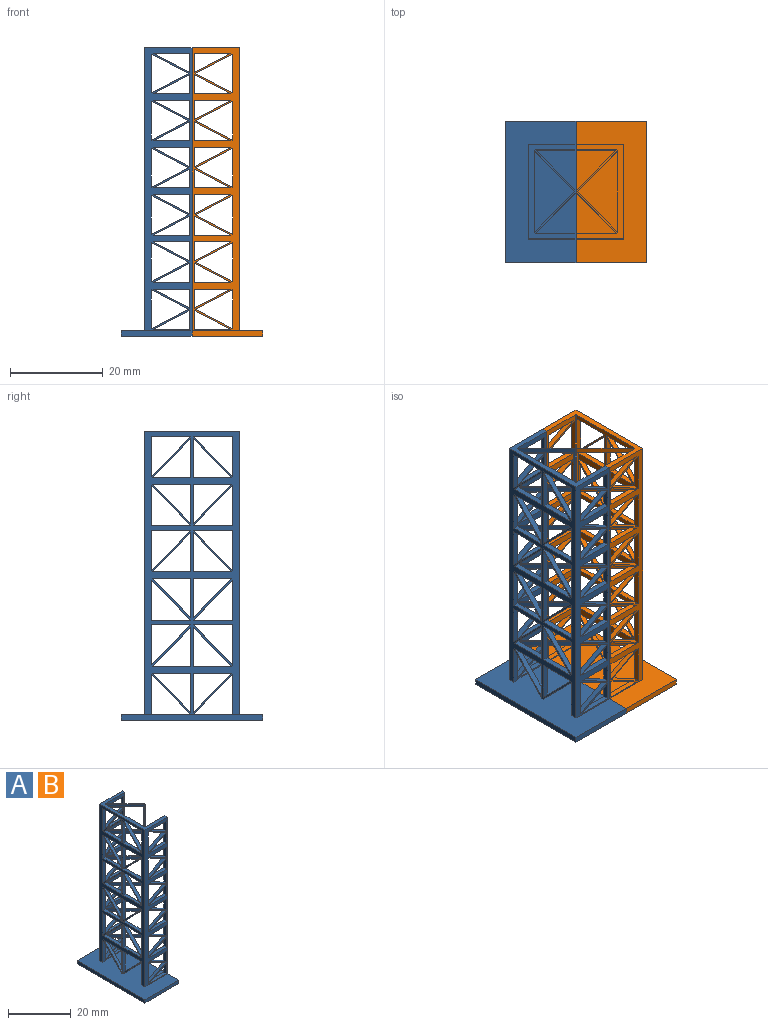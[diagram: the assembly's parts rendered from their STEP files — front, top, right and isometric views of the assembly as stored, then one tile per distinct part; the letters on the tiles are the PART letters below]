
ASSEMBLY  parts=2 mates=1
PART A: 257 faces, bbox 20000000000000000038313501714693374724319102545303840223056070291987586484079775119224722902163606470656x20000000000000000038313501714693374724319102545303840223056070291987586484079775119224722902163606470656x62.2 mm
  f0: plane 7.77x1.16mm, normal (0,0,-1), area 9mm2, adj f1,f253,f254,f255
  f1: plane 60.96x10.16mm, normal (0,1,0), area 227.5mm2, adj f0,f2,f3,f4,f5,f6,f7,f8
  f2: plane 8.02x4.2mm, normal (-0.46,0,0.89), area 10.5mm2, adj f1,f3,f4,f254
  f3: plane 8.4x1.16mm, normal (1,0,0), area 9.7mm2, adj f1,f2,f4,f254
  f4: plane 8.02x4.2mm, normal (-0.46,0,-0.89), area 10.5mm2, adj f1,f2,f3,f254
  f5: plane 8.4x1.16mm, normal (1,0,0), area 9.7mm2, adj f1,f6,f7,f254
  f6: plane 8.02x4.2mm, normal (-0.46,0,-0.89), area 10.5mm2, adj f1,f5,f7,f254
  f7: plane 8.02x4.2mm, normal (-0.46,0,0.89), area 10.5mm2, adj f1,f5,f6,f254
  f8: plane 8.4x1.16mm, normal (1,0,0), area 9.7mm2, adj f1,f9,f10,f254
  f9: plane 8.02x4.2mm, normal (-0.46,0,-0.89), area 10.5mm2, adj f1,f8,f10,f254
  f10: plane 8.02x4.2mm, normal (-0.46,0,0.89), area 10.5mm2, adj f1,f8,f9,f254
  f11: plane 8.4x1.16mm, normal (1,0,0), area 9.7mm2, adj f1,f12,f13,f254
  f12: plane 8.02x4.2mm, normal (-0.46,0,-0.89), area 10.5mm2, adj f1,f11,f13,f254
  f13: plane 8.02x4.2mm, normal (-0.46,0,0.89), area 10.5mm2, adj f1,f11,f12,f254
  f14: plane 8.02x4.2mm, normal (-0.46,0,-0.89), area 10.5mm2, adj f1,f15,f16,f254
  f15: plane 8.02x4.2mm, normal (-0.46,0,0.89), area 10.5mm2, adj f1,f14,f16,f254
  f16: plane 8.4x1.16mm, normal (1,0,0), area 9.7mm2, adj f1,f14,f15,f254
  f17: plane 8.02x4.2mm, normal (-0.46,0,-0.89), area 10.5mm2, adj f1,f18,f19,f254
  f18: plane 8.02x4.2mm, normal (-0.46,0,0.89), area 10.5mm2, adj f1,f17,f19,f254
  f19: plane 8.4x1.16mm, normal (1,0,0), area 9.7mm2, adj f1,f17,f18,f254
  f20: plane 7.77x1.16mm, normal (0,0,1), area 9mm2, adj f1,f21,f22,f254
  f21: plane 7.77x4.07mm, normal (0.46,0,-0.89), area 10.2mm2, adj f1,f20,f22,f254
  f22: plane 4.07x1.16mm, normal (-1,0,0), area 4.7mm2, adj f1,f20,f21,f254
  f23: plane 7.77x1.16mm, normal (0,0,-1), area 9mm2, adj f1,f24,f25,f254
  f24: plane 4.07x1.16mm, normal (-1,0,0), area 4.7mm2, adj f1,f23,f25,f254
  f25: plane 7.77x4.07mm, normal (0.46,0,0.89), area 10.2mm2, adj f1,f23,f24,f254
  f26: plane 7.77x1.16mm, normal (0,0,1), area 9mm2, adj f1,f27,f28,f254
  f27: plane 7.77x4.07mm, normal (0.46,0,-0.89), area 10.2mm2, adj f1,f26,f28,f254
  f28: plane 4.07x1.16mm, normal (-1,0,0), area 4.7mm2, adj f1,f26,f27,f254
  f29: plane 7.77x1.16mm, normal (0,0,-1), area 9mm2, adj f1,f30,f31,f254
  f30: plane 4.07x1.16mm, normal (-1,0,0), area 4.7mm2, adj f1,f29,f31,f254
  f31: plane 7.77x4.07mm, normal (0.46,0,0.89), area 10.2mm2, adj f1,f29,f30,f254
  f32: plane 7.77x1.16mm, normal (0,0,1), area 9mm2, adj f1,f33,f34,f254
  f33: plane 7.77x4.07mm, normal (0.46,0,-0.89), area 10.2mm2, adj f1,f32,f34,f254
  f34: plane 4.07x1.16mm, normal (-1,0,0), area 4.7mm2, adj f1,f32,f33,f254
  f35: plane 7.77x4.07mm, normal (0.46,0,0.89), area 10.2mm2, adj f1,f36,f37,f254
  f36: plane 7.77x1.16mm, normal (0,0,-1), area 9mm2, adj f1,f35,f37,f254
  f37: plane 4.07x1.16mm, normal (-1,0,0), area 4.7mm2, adj f1,f35,f36,f254
  f38: plane 7.77x1.16mm, normal (0,0,1), area 9mm2, adj f1,f39,f40,f254
  f39: plane 7.77x4.07mm, normal (0.46,0,-0.89), area 10.2mm2, adj f1,f38,f40,f254
  f40: plane 4.07x1.16mm, normal (-1,0,0), area 4.7mm2, adj f1,f38,f39,f254
  f41: plane 7.77x1.16mm, normal (0,0,-1), area 9mm2, adj f1,f42,f43,f254
  f42: plane 4.07x1.16mm, normal (-1,0,0), area 4.7mm2, adj f1,f41,f43,f254
  f43: plane 7.77x4.07mm, normal (0.46,0,0.89), area 10.2mm2, adj f1,f41,f42,f254
  f44: plane 7.77x1.16mm, normal (0,0,1), area 9mm2, adj f1,f45,f46,f254
  f45: plane 7.77x4.07mm, normal (0.46,0,-0.89), area 10.2mm2, adj f1,f44,f46,f254
  f46: plane 4.07x1.16mm, normal (-1,0,0), area 4.7mm2, adj f1,f44,f45,f254
  f47: plane 7.77x1.16mm, normal (0,0,-1), area 9mm2, adj f1,f48,f49,f254
  f48: plane 4.07x1.16mm, normal (-1,0,0), area 4.7mm2, adj f1,f47,f49,f254
  f49: plane 7.77x4.07mm, normal (0.46,0,0.89), area 10.2mm2, adj f1,f47,f48,f254
  f50: plane 7.77x4.07mm, normal (0.46,0,-0.89), area 10.2mm2, adj f1,f51,f52,f254
  f51: plane 4.07x1.16mm, normal (-1,0,0), area 4.7mm2, adj f1,f50,f52,f254
  f52: plane 7.77x1.16mm, normal (0,0,1), area 9mm2, adj f1,f50,f51,f254
  f53: plane 20.32x10.16mm, normal (0,0,1), area 53.3mm2, adj f1,f54,f109,f171,f172,f173,f174,f245
  f54: plane 60.96x10.16mm, normal (0,-1,0), area 227.5mm2, adj f53,f55,f56,f57,f58,f59,f60,f61
  f55: plane 8.02x4.2mm, normal (-0.46,0,-0.89), area 10.5mm2, adj f54,f56,f57,f172
  f56: plane 8.4x1.16mm, normal (1,0,0), area 9.7mm2, adj f54,f55,f57,f172
  f57: plane 8.02x4.2mm, normal (-0.46,0,0.89), area 10.5mm2, adj f54,f55,f56,f172
  f58: plane 8.02x4.2mm, normal (-0.46,0,-0.89), area 10.5mm2, adj f54,f59,f60,f172
  f59: plane 8.4x1.16mm, normal (1,0,0), area 9.7mm2, adj f54,f58,f60,f172
  f60: plane 8.02x4.2mm, normal (-0.46,0,0.89), area 10.5mm2, adj f54,f58,f59,f172
  f61: plane 8.4x1.16mm, normal (1,0,0), area 9.7mm2, adj f54,f62,f63,f172
  f62: plane 8.02x4.2mm, normal (-0.46,0,0.89), area 10.5mm2, adj f54,f61,f63,f172
  f63: plane 8.02x4.2mm, normal (-0.46,0,-0.89), area 10.5mm2, adj f54,f61,f62,f172
  f64: plane 8.4x1.16mm, normal (1,0,0), area 9.7mm2, adj f54,f65,f66,f172
  f65: plane 8.02x4.2mm, normal (-0.46,0,0.89), area 10.5mm2, adj f54,f64,f66,f172
  f66: plane 8.02x4.2mm, normal (-0.46,0,-0.89), area 10.5mm2, adj f54,f64,f65,f172
  f67: plane 8.4x1.16mm, normal (1,0,0), area 9.7mm2, adj f54,f68,f69,f172
  f68: plane 8.02x4.2mm, normal (-0.46,0,0.89), area 10.5mm2, adj f54,f67,f69,f172
  f69: plane 8.02x4.2mm, normal (-0.46,0,-0.89), area 10.5mm2, adj f54,f67,f68,f172
  f70: plane 8.02x4.2mm, normal (-0.46,0,0.89), area 10.5mm2, adj f54,f71,f72,f172
  f71: plane 8.02x4.2mm, normal (-0.46,0,-0.89), area 10.5mm2, adj f54,f70,f72,f172
  f72: plane 8.4x1.16mm, normal (1,0,0), area 9.7mm2, adj f54,f70,f71,f172
  f73: plane 7.77x1.16mm, normal (0,0,-1), area 9mm2, adj f54,f74,f75,f172
  f74: plane 7.77x4.07mm, normal (0.46,0,0.89), area 10.2mm2, adj f54,f73,f75,f172
  f75: plane 4.07x1.16mm, normal (-1,0,0), area 4.7mm2, adj f54,f73,f74,f172
  f76: plane 7.77x4.07mm, normal (0.46,0,-0.89), area 10.2mm2, adj f54,f77,f78,f172
  f77: plane 7.77x1.16mm, normal (0,0,1), area 9mm2, adj f54,f76,f78,f172
  f78: plane 4.07x1.16mm, normal (-1,0,0), area 4.7mm2, adj f54,f76,f77,f172
  f79: plane 7.77x1.16mm, normal (0,0,-1), area 9mm2, adj f54,f80,f81,f172
  f80: plane 7.77x4.07mm, normal (0.46,0,0.89), area 10.2mm2, adj f54,f79,f81,f172
  f81: plane 4.07x1.16mm, normal (-1,0,0), area 4.7mm2, adj f54,f79,f80,f172
  f82: plane 7.77x4.07mm, normal (0.46,0,-0.89), area 10.2mm2, adj f54,f83,f84,f172
  f83: plane 7.77x1.16mm, normal (0,0,1), area 9mm2, adj f54,f82,f84,f172
  f84: plane 4.07x1.16mm, normal (-1,0,0), area 4.7mm2, adj f54,f82,f83,f172
  f85: plane 7.77x1.16mm, normal (0,0,-1), area 9mm2, adj f54,f86,f87,f172
  f86: plane 7.77x4.07mm, normal (0.46,0,0.89), area 10.2mm2, adj f54,f85,f87,f172
  f87: plane 4.07x1.16mm, normal (-1,0,0), area 4.7mm2, adj f54,f85,f86,f172
  f88: plane 7.77x4.07mm, normal (0.46,0,-0.89), area 10.2mm2, adj f54,f89,f90,f172
  f89: plane 7.77x1.16mm, normal (0,0,1), area 9mm2, adj f54,f88,f90,f172
  f90: plane 4.07x1.16mm, normal (-1,0,0), area 4.7mm2, adj f54,f88,f89,f172
  f91: plane 7.77x1.16mm, normal (0,0,-1), area 9mm2, adj f54,f92,f93,f172
  f92: plane 7.77x4.07mm, normal (0.46,0,0.89), area 10.2mm2, adj f54,f91,f93,f172
  f93: plane 4.07x1.16mm, normal (-1,0,0), area 4.7mm2, adj f54,f91,f92,f172
  f94: plane 7.77x4.07mm, normal (0.46,0,-0.89), area 10.2mm2, adj f54,f95,f96,f172
  f95: plane 7.77x1.16mm, normal (0,0,1), area 9mm2, adj f54,f94,f96,f172
  f96: plane 4.07x1.16mm, normal (-1,0,0), area 4.7mm2, adj f54,f94,f95,f172
  f97: plane 7.77x1.16mm, normal (0,0,-1), area 9mm2, adj f54,f98,f99,f172
  f98: plane 7.77x4.07mm, normal (0.46,0,0.89), area 10.2mm2, adj f54,f97,f99,f172
  f99: plane 4.07x1.16mm, normal (-1,0,0), area 4.7mm2, adj f54,f97,f98,f172
  f100: plane 7.77x4.07mm, normal (0.46,0,-0.89), area 10.2mm2, adj f54,f101,f102,f172
  f101: plane 7.77x1.16mm, normal (0,0,1), area 9mm2, adj f54,f100,f102,f172
  f102: plane 4.07x1.16mm, normal (-1,0,0), area 4.7mm2, adj f54,f100,f101,f172
  f103: plane 7.77x4.07mm, normal (0.46,0,-0.89), area 10.2mm2, adj f54,f104,f105,f172
  f104: plane 7.77x1.16mm, normal (0,0,1), area 9mm2, adj f54,f103,f105,f172
  f105: plane 4.07x1.16mm, normal (-1,0,0), area 4.7mm2, adj f54,f103,f104,f172
  f106: plane 7.77x4.07mm, normal (0.46,0,0.89), area 10.2mm2, adj f54,f107,f108,f172
  f107: plane 4.07x1.16mm, normal (-1,0,0), area 4.7mm2, adj f54,f106,f108,f172
  f108: plane 7.77x1.16mm, normal (0,0,-1), area 9mm2, adj f54,f106,f107,f172
  f109: plane 8.75x8.75mm, normal (0.71,0.71,0), area 12.4mm2, adj f53,f110,f252,f254
  f110: plane 9x8.75mm, normal (0,0,-1), area 4.3mm2, adj f109,f111,f173,f174,f254
  f111: plane 9.16x0.5mm, normal (0,1,0), area 4.6mm2, adj f110,f112,f170,f252
  f112: plane 9.16x0.25mm, normal (-0.71,-0.71,0), area 3.2mm2, adj f111,f113,f169,f173
  f113: plane 9.16x0.25mm, normal (-0.71,0.71,0), area 3.2mm2, adj f112,f114,f168,f245
  f114: plane 59.96x0.5mm, normal (0,-1,0), area 27.5mm2, adj f113,f115,f116,f117,f118,f151,f152,f153
  f115: plane 8.75x8.75mm, normal (0.71,-0.71,0), area 12.4mm2, adj f114,f116,f167,f172
  f116: plane 9x8.75mm, normal (0,0,1), area 4.3mm2, adj f114,f115,f168,f172,f174
  f117: plane 9x8.75mm, normal (0,0,-1), area 4.3mm2, adj f114,f171,f172,f174,f245
  f118: plane 9.16x0.25mm, normal (-0.71,0.71,0), area 3.2mm2, adj f114,f119,f150,f247
  f119: plane 9.16x0.25mm, normal (-0.71,-0.71,0), area 3.2mm2, adj f118,f120,f149,f247
  f120: plane 9.16x0.5mm, normal (0,1,0), area 4.6mm2, adj f119,f121,f247,f252
  f121: plane 9x8.75mm, normal (0,0,-1), area 4.3mm2, adj f120,f122,f149,f174,f254
  f122: plane 8.75x8.75mm, normal (0.71,0.71,0), area 12.4mm2, adj f121,f123,f252,f254
  f123: plane 9x8.75mm, normal (0,0,1), area 4.3mm2, adj f122,f124,f149,f174,f254
  f124: plane 9.16x0.5mm, normal (0,1,0), area 4.6mm2, adj f123,f125,f148,f252
  f125: plane 9x8.75mm, normal (0,0,-1), area 4.3mm2, adj f124,f126,f147,f174,f254
  f126: plane 8.75x8.75mm, normal (-0.71,-0.71,0), area 12.4mm2, adj f125,f127,f145,f146,f148,f174
  f127: plane 9x8.75mm, normal (0,0,1), area 4.3mm2, adj f126,f128,f147,f174,f254
  f128: plane 9.16x0.5mm, normal (0,1,0), area 4.6mm2, adj f127,f129,f145,f252
  f129: plane 9x8.75mm, normal (0,0,-1), area 4.3mm2, adj f128,f130,f144,f174,f254
  f130: plane 8.75x8.75mm, normal (-0.71,-0.71,0), area 12.4mm2, adj f129,f131,f142,f143,f145,f174
  f131: plane 9x8.75mm, normal (0,0,1), area 4.3mm2, adj f130,f132,f144,f174,f254
  f132: plane 9.16x0.5mm, normal (0,1,0), area 4.6mm2, adj f131,f133,f142,f252
  f133: plane 9x8.75mm, normal (0,0,-1), area 4.3mm2, adj f132,f134,f141,f174,f254
  f134: plane 8.75x8.75mm, normal (-0.71,-0.71,0), area 12.4mm2, adj f133,f135,f139,f140,f142,f174
  f135: plane 9x8.75mm, normal (0,0,1), area 4.3mm2, adj f134,f136,f141,f174,f254
  f136: plane 9.16x0.5mm, normal (0,1,0), area 4.6mm2, adj f135,f137,f139,f252
  f137: plane 9x8.75mm, normal (0,0,-1), area 4.3mm2, adj f136,f138,f169,f174,f254
  f138: plane 8.75x8.75mm, normal (0.71,0.71,0), area 12.4mm2, adj f137,f170,f252,f254
  f139: plane 9.16x0.25mm, normal (-0.71,-0.71,0), area 3.2mm2, adj f134,f136,f166,f169
  f140: plane 8.75x8.75mm, normal (-0.71,0.71,0), area 12.4mm2, adj f134,f162,f163,f165,f166,f174
  f141: plane 8.75x8.75mm, normal (0.71,0.71,0), area 12.4mm2, adj f133,f135,f252,f254
  f142: plane 9.16x0.25mm, normal (-0.71,-0.71,0), area 3.2mm2, adj f130,f132,f134,f162
  f143: plane 8.75x8.75mm, normal (-0.71,0.71,0), area 12.4mm2, adj f130,f158,f159,f161,f162,f174
  f144: plane 8.75x8.75mm, normal (0.71,0.71,0), area 12.4mm2, adj f129,f131,f252,f254
  f145: plane 9.16x0.25mm, normal (-0.71,-0.71,0), area 3.2mm2, adj f126,f128,f130,f158
  f146: plane 8.75x8.75mm, normal (-0.71,0.71,0), area 12.4mm2, adj f126,f154,f155,f157,f158,f174
  f147: plane 8.75x8.75mm, normal (0.71,0.71,0), area 12.4mm2, adj f125,f127,f252,f254
  f148: plane 9.16x0.25mm, normal (-0.71,-0.71,0), area 3.2mm2, adj f124,f126,f149,f154
  f149: plane 8.75x8.75mm, normal (-0.71,-0.71,0), area 12.4mm2, adj f119,f121,f123,f148,f150,f174
  f150: plane 8.75x8.75mm, normal (-0.71,0.71,0), area 12.4mm2, adj f118,f149,f151,f153,f154,f174
  f151: plane 9x8.75mm, normal (0,0,-1), area 4.3mm2, adj f114,f150,f152,f172,f174
  f152: plane 8.75x8.75mm, normal (0.71,-0.71,0), area 12.4mm2, adj f114,f151,f153,f172
  f153: plane 9x8.75mm, normal (0,0,1), area 4.3mm2, adj f114,f150,f152,f172,f174
  f154: plane 9.16x0.25mm, normal (-0.71,0.71,0), area 3.2mm2, adj f114,f146,f148,f150
  f155: plane 9x8.75mm, normal (0,0,-1), area 4.3mm2, adj f114,f146,f156,f172,f174
  f156: plane 8.75x8.75mm, normal (0.71,-0.71,0), area 12.4mm2, adj f114,f155,f157,f172
  f157: plane 9x8.75mm, normal (0,0,1), area 4.3mm2, adj f114,f146,f156,f172,f174
  f158: plane 9.16x0.25mm, normal (-0.71,0.71,0), area 3.2mm2, adj f114,f143,f145,f146
  f159: plane 9x8.75mm, normal (0,0,-1), area 4.3mm2, adj f114,f143,f160,f172,f174
  f160: plane 8.75x8.75mm, normal (0.71,-0.71,0), area 12.4mm2, adj f114,f159,f161,f172
  f161: plane 9x8.75mm, normal (0,0,1), area 4.3mm2, adj f114,f143,f160,f172,f174
  f162: plane 9.16x0.25mm, normal (-0.71,0.71,0), area 3.2mm2, adj f114,f140,f142,f143
  f163: plane 9x8.75mm, normal (0,0,-1), area 4.3mm2, adj f114,f140,f164,f172,f174
  f164: plane 8.75x8.75mm, normal (0.71,-0.71,0), area 12.4mm2, adj f114,f163,f165,f172
  f165: plane 9x8.75mm, normal (0,0,1), area 4.3mm2, adj f114,f140,f164,f172,f174
  f166: plane 9.16x0.25mm, normal (-0.71,0.71,0), area 3.2mm2, adj f114,f139,f140,f168
  f167: plane 9x8.75mm, normal (0,0,-1), area 4.3mm2, adj f114,f115,f168,f172,f174
  f168: plane 8.75x8.75mm, normal (-0.71,0.71,0), area 12.4mm2, adj f113,f116,f166,f167,f169,f174
  f169: plane 8.75x8.75mm, normal (-0.71,-0.71,0), area 12.4mm2, adj f112,f137,f139,f168,f170,f174
  f170: plane 9x8.75mm, normal (0,0,1), area 4.3mm2, adj f111,f138,f169,f174,f254
  f171: plane 8.75x8.75mm, normal (0.71,-0.71,0), area 12.4mm2, adj f53,f117,f172,f252
  f172: plane 60.96x9mm, normal (0,1,0), area 155.3mm2, adj f53,f55,f56,f57,f58,f59,f60,f61
  f173: plane 8.75x8.75mm, normal (-0.71,-0.71,0), area 12.4mm2, adj f53,f110,f112,f174,f245
  f174: plane 60.96x18mm, normal (1,0,0), area 236.3mm2, adj f53,f110,f116,f117,f121,f123,f125,f126
  f175: plane 8.41x8.25mm, normal (0,-0.71,-0.7), area 13.7mm2, adj f174,f176,f177,f246
  f176: plane 8.41x1.16mm, normal (0,1,0), area 9.8mm2, adj f174,f175,f177,f246
  f177: plane 8.25x1.16mm, normal (0,0,1), area 9.6mm2, adj f174,f175,f176,f246
  f178: plane 8.25x1.16mm, normal (0,0,-1), area 9.6mm2, adj f174,f179,f180,f246
  f179: plane 8.41x1.16mm, normal (0,1,0), area 9.8mm2, adj f174,f178,f180,f246
  f180: plane 8.41x8.25mm, normal (0,-0.71,0.7), area 13.7mm2, adj f174,f178,f179,f246
  f181: plane 8.41x8.25mm, normal (0,-0.71,-0.7), area 13.7mm2, adj f174,f182,f183,f246
  f182: plane 8.41x1.16mm, normal (0,1,0), area 9.8mm2, adj f174,f181,f183,f246
  f183: plane 8.25x1.16mm, normal (0,0,1), area 9.6mm2, adj f174,f181,f182,f246
  f184: plane 8.25x1.16mm, normal (0,0,-1), area 9.6mm2, adj f174,f185,f186,f246
  f185: plane 8.41x1.16mm, normal (0,1,0), area 9.8mm2, adj f174,f184,f186,f246
  f186: plane 8.41x8.25mm, normal (0,-0.71,0.7), area 13.7mm2, adj f174,f184,f185,f246
  f187: plane 8.41x8.25mm, normal (0,-0.71,-0.7), area 13.7mm2, adj f174,f188,f189,f246
  f188: plane 8.41x1.16mm, normal (0,1,0), area 9.8mm2, adj f174,f187,f189,f246
  f189: plane 8.25x1.16mm, normal (0,0,1), area 9.6mm2, adj f174,f187,f188,f246
  f190: plane 8.25x1.16mm, normal (0,0,-1), area 9.6mm2, adj f174,f191,f192,f246
  f191: plane 8.41x1.16mm, normal (0,1,0), area 9.8mm2, adj f174,f190,f192,f246
  f192: plane 8.41x8.25mm, normal (0,-0.71,0.7), area 13.7mm2, adj f174,f190,f191,f246
  f193: plane 8.66x1.16mm, normal (0,-1,0), area 10mm2, adj f174,f194,f246,f247
  f194: plane 8.66x8.5mm, normal (0,0.71,-0.7), area 14.1mm2, adj f174,f193,f246,f247
  f195: plane 8.66x8.5mm, normal (0,-0.71,-0.7), area 14.1mm2, adj f174,f196,f246,f247
  f196: plane 8.66x1.16mm, normal (0,1,0), area 10mm2, adj f174,f195,f246,f247
  f197: plane 8.66x1.16mm, normal (0,1,0), area 10mm2, adj f174,f198,f199,f246
  f198: plane 8.5x1.16mm, normal (0,0,1), area 9.9mm2, adj f174,f197,f199,f246
  f199: plane 8.66x8.5mm, normal (0,-0.71,-0.7), area 14.1mm2, adj f174,f197,f198,f246
  f200: plane 8.66x1.16mm, normal (0,1,0), area 10mm2, adj f174,f201,f202,f246
  f201: plane 8.66x8.5mm, normal (0,-0.71,0.7), area 14.1mm2, adj f174,f200,f202,f246
  f202: plane 8.5x1.16mm, normal (0,0,-1), area 9.9mm2, adj f174,f200,f201,f246
  f203: plane 8.5x1.16mm, normal (0,0,1), area 9.9mm2, adj f174,f204,f205,f246
  f204: plane 8.66x8.5mm, normal (0,-0.71,-0.7), area 14.1mm2, adj f174,f203,f205,f246
  f205: plane 8.66x1.16mm, normal (0,1,0), area 10mm2, adj f174,f203,f204,f246
  f206: plane 8.66x1.16mm, normal (0,1,0), area 10mm2, adj f174,f207,f208,f246
  f207: plane 8.66x8.5mm, normal (0,-0.71,0.7), area 14.1mm2, adj f174,f206,f208,f246
  f208: plane 8.5x1.16mm, normal (0,0,-1), area 9.9mm2, adj f174,f206,f207,f246
  f209: plane 8.5x1.16mm, normal (0,0,-1), area 9.9mm2, adj f174,f210,f211,f246
  f210: plane 8.66x8.5mm, normal (0,0.71,0.7), area 14.1mm2, adj f174,f209,f211,f246
  f211: plane 8.66x1.16mm, normal (0,-1,0), area 10mm2, adj f174,f209,f210,f246
  f212: plane 8.66x1.16mm, normal (0,-1,0), area 10mm2, adj f174,f213,f214,f246
  f213: plane 8.66x8.5mm, normal (0,0.71,-0.7), area 14.1mm2, adj f174,f212,f214,f246
  f214: plane 8.5x1.16mm, normal (0,0,1), area 9.9mm2, adj f174,f212,f213,f246
  f215: plane 8.5x1.16mm, normal (0,0,-1), area 9.9mm2, adj f174,f216,f217,f246
  f216: plane 8.66x8.5mm, normal (0,0.71,0.7), area 14.1mm2, adj f174,f215,f217,f246
  f217: plane 8.66x1.16mm, normal (0,-1,0), area 10mm2, adj f174,f215,f216,f246
  f218: plane 8.66x1.16mm, normal (0,-1,0), area 10mm2, adj f174,f219,f220,f246
  f219: plane 8.66x8.5mm, normal (0,0.71,-0.7), area 14.1mm2, adj f174,f218,f220,f246
  f220: plane 8.5x1.16mm, normal (0,0,1), area 9.9mm2, adj f174,f218,f219,f246
  f221: plane 8.5x1.16mm, normal (0,0,-1), area 9.9mm2, adj f174,f222,f223,f246
  f222: plane 8.66x8.5mm, normal (0,0.71,0.7), area 14.1mm2, adj f174,f221,f223,f246
  f223: plane 8.66x1.16mm, normal (0,-1,0), area 10mm2, adj f174,f221,f222,f246
  f224: plane 8.66x1.16mm, normal (0,1,0), area 10mm2, adj f174,f225,f226,f246
  f225: plane 8.66x8.5mm, normal (0,-0.71,0.7), area 14.1mm2, adj f174,f224,f226,f246
  f226: plane 8.5x1.16mm, normal (0,0,-1), area 9.9mm2, adj f174,f224,f225,f246
  f227: plane 8.41x8.26mm, normal (0,0.71,-0.7), area 13.7mm2, adj f174,f228,f229,f246
  f228: plane 8.26x1.16mm, normal (0,0,1), area 9.6mm2, adj f174,f227,f229,f246
  f229: plane 8.41x1.16mm, normal (0,-1,0), area 9.8mm2, adj f174,f227,f228,f246
  f230: plane 8.26x1.16mm, normal (0,0,-1), area 9.6mm2, adj f174,f231,f232,f246
  f231: plane 8.41x8.26mm, normal (0,0.71,0.7), area 13.7mm2, adj f174,f230,f232,f246
  f232: plane 8.41x1.16mm, normal (0,-1,0), area 9.8mm2, adj f174,f230,f231,f246
  f233: plane 8.41x8.26mm, normal (0,0.71,-0.7), area 13.7mm2, adj f174,f234,f235,f246
  f234: plane 8.26x1.16mm, normal (0,0,1), area 9.6mm2, adj f174,f233,f235,f246
  f235: plane 8.41x1.16mm, normal (0,-1,0), area 9.8mm2, adj f174,f233,f234,f246
  f236: plane 8.26x1.16mm, normal (0,0,-1), area 9.6mm2, adj f174,f237,f238,f246
  f237: plane 8.41x8.26mm, normal (0,0.71,0.7), area 13.7mm2, adj f174,f236,f238,f246
  f238: plane 8.41x1.16mm, normal (0,-1,0), area 9.8mm2, adj f174,f236,f237,f246
  f239: plane 8.41x8.26mm, normal (0,0.71,-0.7), area 13.7mm2, adj f174,f240,f241,f246
  f240: plane 8.26x1.16mm, normal (0,0,1), area 9.6mm2, adj f174,f239,f241,f246
  f241: plane 8.41x1.16mm, normal (0,-1,0), area 9.8mm2, adj f174,f239,f240,f246
  f242: plane 8.26x1.16mm, normal (0,0,-1), area 9.6mm2, adj f174,f243,f244,f246
  f243: plane 8.41x8.26mm, normal (0,0.71,0.7), area 13.7mm2, adj f174,f242,f244,f246
  f244: plane 8.41x1.16mm, normal (0,-1,0), area 9.8mm2, adj f174,f242,f243,f246
  f245: plane 8.75x8.75mm, normal (-0.71,0.71,0), area 12.4mm2, adj f53,f113,f117,f173,f174
  f246: plane 60.96x20.32mm, normal (-1,0,0), area 380.8mm2, adj f1,f53,f54,f175,f176,f177,f178,f179
  f247: plane 30.48x15.24mm, normal (0,0,1), area 439.6mm2, adj f1,f54,f114,f118,f119,f120,f172,f174
  f248: plane 15.24x1.27mm, normal (0,-1,0), area 19.4mm2, adj f247,f249,f250,f252
  f249: plane 30.48x15.24mm, normal (0,0,-1), area 464.5mm2, adj f248,f250,f251,f252
  f250: plane 30.48x1.27mm, normal (-1,0,0), area 38.7mm2, adj f247,f248,f249,f251
  f251: plane 15.24x1.27mm, normal (0,1,0), area 19.4mm2, adj f247,f249,f250,f252
  f252: plane 62.23x30.48mm, normal (1,0,0), area 210.6mm2, adj f1,f53,f54,f109,f111,f114,f120,f122
  f253: plane 7.77x4.07mm, normal (0.46,0,0.89), area 10.2mm2, adj f0,f1,f254,f255
  f254: plane 60.96x9mm, normal (0,-1,0), area 155.3mm2, adj f0,f2,f3,f4,f5,f6,f7,f8
  f255: plane 4.07x1.16mm, normal (-1,0,0), area 4.7mm2, adj f0,f1,f253,f254
  f256: plane 20000000000000000038313501714693374724319102545303840223056070291987586484079775119224722902163606470656x20000000000000000038313501714693374724319102545303840223056070291987586484079775119224722902163606470656mm, normal (0,0,1), area 80000000000000007282879924029474800836836319614038924572363658998727223162810673217233440780332897524514816mm2
PART B: same geometry as A
PLACE A t=(-28.74,-9.56,0.47)mm
PLACE B rot(axis=(0,0,1),180deg) t=(-28.74,-9.56,0.47)mm
MATE fastened B.f252 <-> A.f252  axis (-1,0,0) through (-28.74,-9.56,26.5)mm
